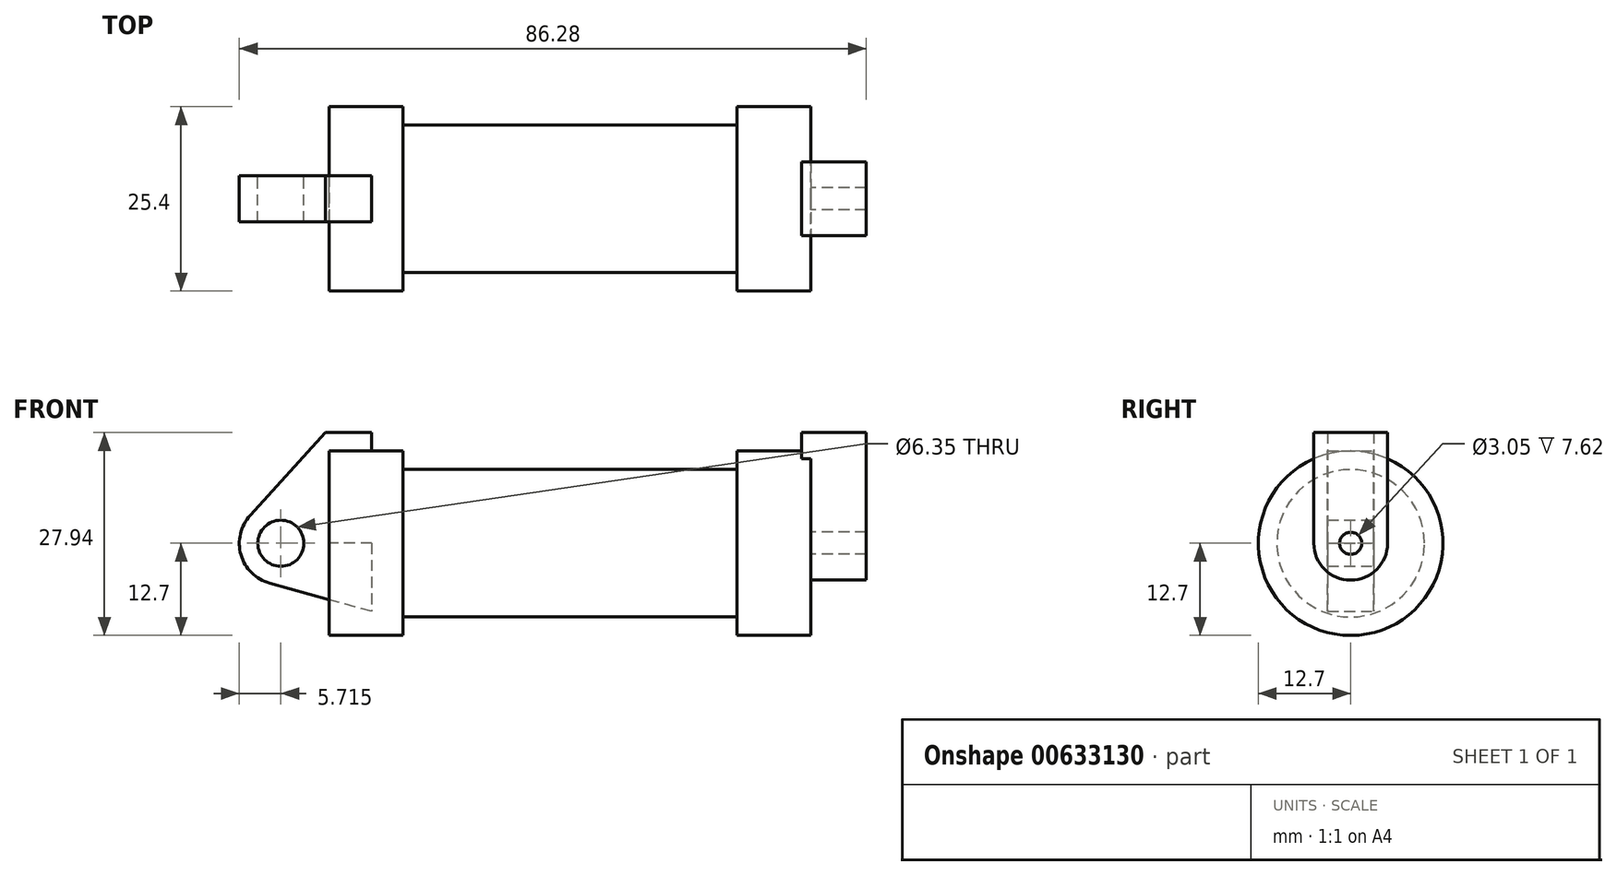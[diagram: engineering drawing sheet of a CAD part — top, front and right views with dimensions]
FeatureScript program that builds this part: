
annotation { "Feature Type Name" : "Feature", "Feature Type Description" : "" }
export const myFeature = defineFeature(function(context is Context, id is Id, definition is map)
    precondition{}
    {
        {
            var Q0;
            Q0=qCreatedBy(makeId("Front.planeOp"),FACE);
            var sketch = newSketch(context, id + "F0", { "sketchPlane" : qUnion([Q0])});
            skLineSegment(sketch, "E0", {"start": v(0, 0) * mm, "end": v(0, 12.7) * mm});
            skLineSegment(sketch, "E1", {"start": v(0, 12.7) * mm, "end": v(10.16, 12.7) * mm});
            skLineSegment(sketch, "E2", {"start": v(10.16, 12.7) * mm, "end": v(10.16, 10.16) * mm});
            skLineSegment(sketch, "E3", {"start": v(10.16, 10.16) * mm, "end": v(56.13, 10.16) * mm});
            skLineSegment(sketch, "E4", {"start": v(56.13, 10.16) * mm, "end": v(56.13, 12.7) * mm});
            skLineSegment(sketch, "E5", {"start": v(56.13, 12.7) * mm, "end": v(66.3, 12.7) * mm});
            skLineSegment(sketch, "E6", {"start": v(66.3, 12.7) * mm, "end": v(66.3, 0) * mm});
            skLineSegment(sketch, "E7", {"start": v(66.3, 0) * mm, "end": v(0, 0) * mm});
            skLineSegment(sketch, "E8", {"start": v(5.84, 15.24) * mm, "end": v(-0.5, 15.24) * mm});
            skLineSegment(sketch, "E9", {"start": v(-0.5, 15.24) * mm, "end": v(-10.88, 3.85) * mm});
            skLineSegment(sketch, "E10", {"start": v(0, 0) * mm, "end": v(-6.65, 0) * mm});
            skCircle(sketch, "E11", {"center": v(-6.65, 0) * mm, "radius": 5.72 * mm});
            skCircle(sketch, "E12", {"center": v(-6.65, 0) * mm, "radius": 3.18 * mm});
            skLineSegment(sketch, "E13", {"start": v(5.84, 15.24) * mm, "end": v(5.84, -9.4) * mm});
            skLineSegment(sketch, "E14", {"start": v(5.84, -9.4) * mm, "end": v(-8.18, -5.5) * mm});
            skSolve(sketch);
        }
        {
            var Q0;
            {var subQ0=sQuery(id+"F0.wireOp",EDGE,"E0");Q0=makeQuery(id+"F0.imprint","IMPRINT",FACE,{"disambiguationData":[TD([[makeQuery(id+"F0.imprint","IMPRINT",EDGE,{"derivedFrom":subQ0}),-1.0]])]});}
            var Q1;
            {var subQ0=sQuery(id+"F0.wireOp",EDGE,"E2");Q1=makeQuery(id+"F0.imprint","IMPRINT",FACE,{"disambiguationData":[TD([[makeQuery(id+"F0.imprint","IMPRINT",EDGE,{"derivedFrom":subQ0}),-1.0]])]});}
            var Q2;
            Q2=sQuery(id+"F0.wireOp",EDGE,"E7");
            revolve(context, id + "F1", {"entities" : qUnion([Q0, Q1]), "axis" : qUnion([Q2]), "revolveType" : RevolveType.FULL});
        }
        {
            var Q0;
            {var subQ5=sQuery(id+"F0.wireOp",EDGE,"E12");Q0=makeQuery(id+"F0.imprint","IMPRINT",FACE,{"disambiguationData":[TD([[makeQuery(id+"F0.imprint","IMPRINT",EDGE,{"derivedFrom":subQ5}),-1.0]])]});}
            var Q1;
            {var subQ1=sQuery(id+"F0.wireOp",EDGE,"E0");Q1=makeQuery(id+"F0.imprint","IMPRINT",FACE,{"disambiguationData":[TD([[makeQuery(id+"F0.imprint","IMPRINT",EDGE,{"derivedFrom":subQ1}),1.0]])]});}
            var Q2;
            {var subQ0=sQuery(id+"F0.wireOp",EDGE,"E14");Q2=makeQuery(id+"F0.imprint","IMPRINT",FACE,{"disambiguationData":[TD([[makeQuery(id+"F0.imprint","IMPRINT",EDGE,{"derivedFrom":subQ0}),-1.0]])]});}
            extrude(context, id + "F2", {"entities" : qUnion([Q0, Q1, Q2]), "endBound" : BoundingType.SYMMETRIC, "depth" : 6.35 * mm, "offsetDistance" : 25.4 * mm});
        }
        {
            var Q0;
            Q0=makeQuery(id+"F1.opRevolve","SWEPT_FACE",FACE,{"disambiguationData":[OSD([sQuery(id+"F0.wireOp",EDGE,"E6")])]});
            var sketch = newSketch(context, id + "F3", { "sketchPlane" : qUnion([Q0])});
            skCircle(sketch, "E15", {"center": v(0, 0) * mm, "radius": 1.52 * mm});
            skCircle(sketch, "E16", {"center": v(0, 0) * mm, "radius": 5.08 * mm});
            skLineSegment(sketch, "E17", {"start": v(5.08, 0) * mm, "end": v(5.08, 15.24) * mm});
            skLineSegment(sketch, "E18", {"start": v(-5.08, 0) * mm, "end": v(-5.08, 15.24) * mm});
            skLineSegment(sketch, "E19", {"start": v(-5.08, 15.24) * mm, "end": v(5.08, 15.24) * mm});
            skLineSegment(sketch, "E20", {"start": v(1.04, 3.69) * mm, "end": v(-0.56, 1.73) * mm});
            skSolve(sketch);
        }
        {
            var Q0;
            {var subQ0=sQuery(id+"F3.wireOp",EDGE,"E17");var subQ1=sQuery(id+"F3.wireOp",EDGE,"E16");var subQ2=makeQuery(id+"F3.imprint","INTERSECT",VERTEX,{"derivedFrom":[subQ1,subQ0]});Q0=makeQuery(id+"F3.imprint","IMPRINT",FACE,{"disambiguationData":[TD([[makeQuery(id+"F3.imprint","IMPRINT",EDGE,{"disambiguationData":[TD([[subQ2,-1.0]])],"derivedFrom":subQ1}),-1.0]])]});}
            var Q1;
            {var subQ0=sQuery(id+"F3.wireOp",EDGE,"E19");Q1=makeQuery(id+"F3.imprint","IMPRINT",FACE,{"disambiguationData":[TD([[makeQuery(id+"F3.imprint","IMPRINT",EDGE,{"derivedFrom":subQ0}),-1.0]])]});}
            var Q2;
            Q2=makeQuery(id+"F3.imprint","IMPRINT",FACE,{"disambiguationData":[TD([[makeQuery(id+"F3.imprint","IMPRINT",EDGE,{"derivedFrom":sQuery(id+"F3.wireOp",EDGE,"E15")}),-1.0]])]});
            extrude(context, id + "F4", {"entities" : qUnion([Q0, Q1, Q2]), "operationType" : NewBodyOperationType.ADD, "depth" : 7.62 * mm, "offsetDistance" : 25.4 * mm, "hasSecondDirection" : true, "secondDirectionOppositeDirection" : true, "secondDirectionDepth" : 1.27 * mm});
        }
    });
